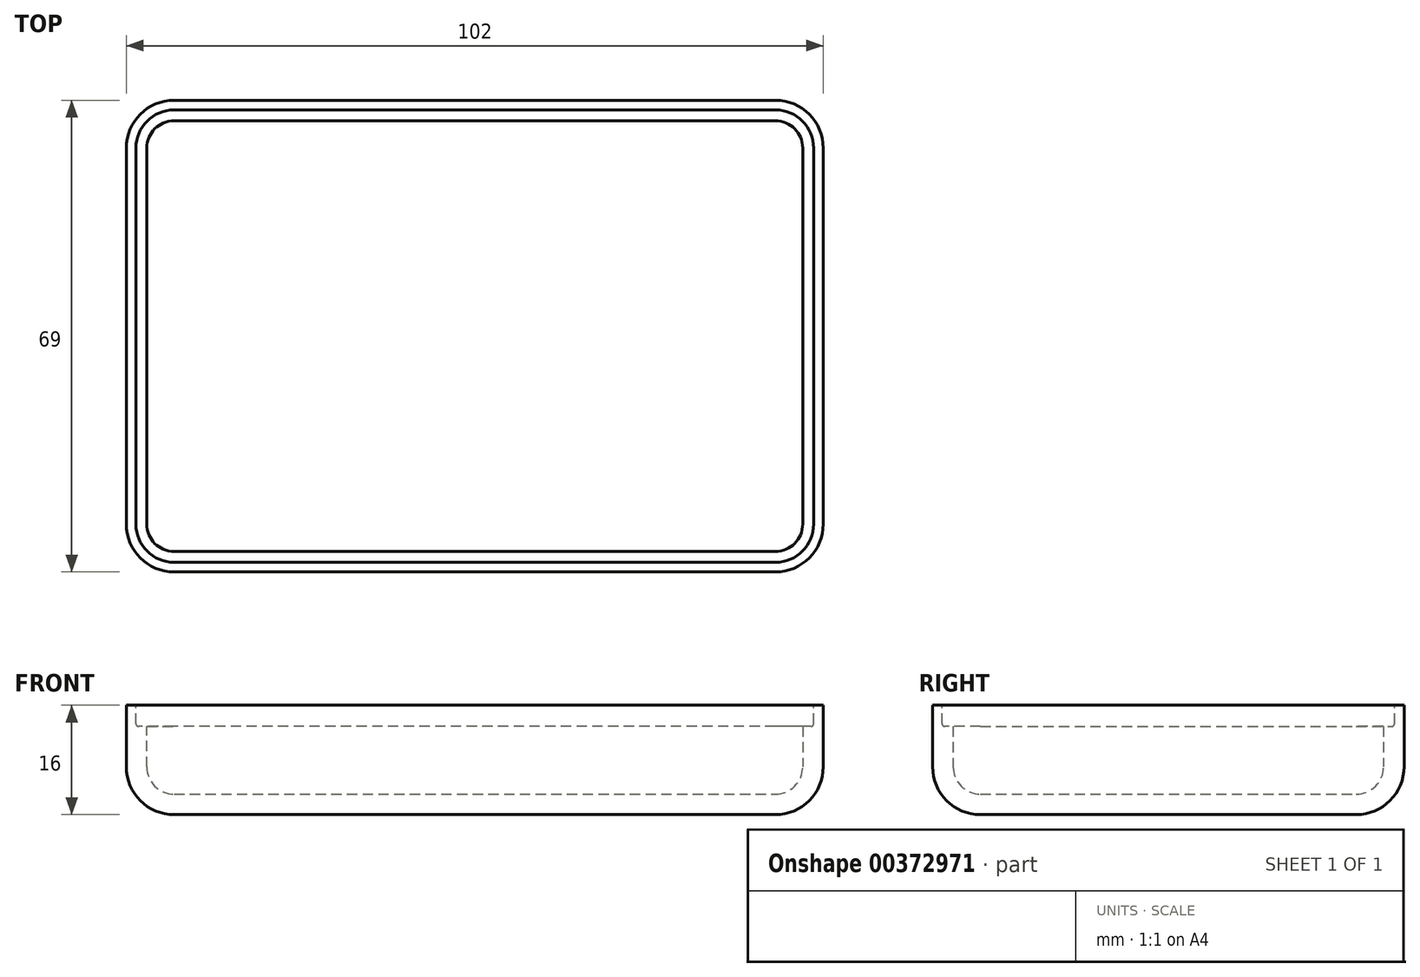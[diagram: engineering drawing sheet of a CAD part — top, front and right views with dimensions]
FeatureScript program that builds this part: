
annotation { "Feature Type Name" : "Feature", "Feature Type Description" : "" }
export const myFeature = defineFeature(function(context is Context, id is Id, definition is map)
    precondition{}
    {
        {
            var Q0;
            Q0=qCreatedBy(makeId("Top.planeOp"),FACE);
            var sketch = newSketch(context, id + "F0", { "sketchPlane" : qUnion([Q0])});
            skLineSegment(sketch, "E0.bottom", {"start": v(44, -34.5) * mm, "end": v(-44, -34.5) * mm});
            skLineSegment(sketch, "E0.top", {"start": v(44, 34.5) * mm, "end": v(-44, 34.5) * mm});
            skLineSegment(sketch, "E0.left", {"start": v(51, -27.5) * mm, "end": v(51, 27.5) * mm});
            skLineSegment(sketch, "E0.right", {"start": v(-51, -27.5) * mm, "end": v(-51, 27.5) * mm});
            skPoint(sketch, "E0.middle", {"position": v(0, 0) * mm});
            skLineSegment(sketch, "E1.bottom", {"start": v(-44, 27.5) * mm, "end": v(44, 27.5) * mm, "construction": true});
            skLineSegment(sketch, "E1.top", {"start": v(-44, -27.5) * mm, "end": v(44, -27.5) * mm, "construction": true});
            skLineSegment(sketch, "E1.left", {"start": v(-44, 27.5) * mm, "end": v(-44, -27.5) * mm, "construction": true});
            skLineSegment(sketch, "E1.right", {"start": v(44, 27.5) * mm, "end": v(44, -27.5) * mm, "construction": true});
            skPoint(sketch, "E2.visualSharp", {"position": v(-51, 34.5) * mm});
            skArc(sketch, "E2.filletArc", {"start": v(-44, 34.5) * mm, "mid": v(-48.95, 32.45) * mm, "end": v(-51, 27.5) * mm});
            skPoint(sketch, "E3.visualSharp", {"position": v(-51, -34.5) * mm});
            skArc(sketch, "E3.filletArc", {"start": v(-51, -27.5) * mm, "mid": v(-48.95, -32.45) * mm, "end": v(-44, -34.5) * mm});
            skPoint(sketch, "E4.visualSharp", {"position": v(51, -34.5) * mm});
            skArc(sketch, "E4.filletArc", {"start": v(44, -34.5) * mm, "mid": v(48.95, -32.45) * mm, "end": v(51, -27.5) * mm});
            skPoint(sketch, "E5.visualSharp", {"position": v(51, 34.5) * mm});
            skArc(sketch, "E5.filletArc", {"start": v(51, 27.5) * mm, "mid": v(48.95, 32.45) * mm, "end": v(44, 34.5) * mm});
            skSolve(sketch);
        }
        {
            var Q0;
            Q0=makeQuery(id+"F0.imprint","IMPRINT",FACE,{"disambiguationData":[TD([[makeQuery(id+"F0.imprint","IMPRINT",EDGE,{"derivedFrom":sQuery(id+"F0.wireOp",EDGE,"E0.bottom")}),-1.0]])]});
            extrude(context, id + "F1", {"entities" : qUnion([Q0]), "depth" : 16 * mm});
        }
        {
            var Q0;
            Q0=makeQuery(id+"F1.opExtrude","CAP_EDGE",EDGE,{"disambiguationData":[OSD([sQuery(id+"F0.wireOp",EDGE,"E0.bottom")])],"isStart":true});
            fillet(context, id + "F2", {"entities" : qUnion([Q0]), "radius" : 7 * mm, "tangentPropagation" : true, "allowEdgeOverflow" : false});
        }
        {
            var Q0;
            Q0=makeQuery(id+"F1.opExtrude","CAP_FACE",FACE,{"disambiguationData":[OSD([sQuery(id+"F0.wireOp",EDGE,"E0.bottom"),sQuery(id+"F0.wireOp",EDGE,"E0.top"),sQuery(id+"F0.wireOp",EDGE,"E0.left"),sQuery(id+"F0.wireOp",EDGE,"E0.right"),sQuery(id+"F0.wireOp",EDGE,"E2.filletArc"),sQuery(id+"F0.wireOp",EDGE,"E3.filletArc"),sQuery(id+"F0.wireOp",EDGE,"E4.filletArc"),sQuery(id+"F0.wireOp",EDGE,"E5.filletArc")])],"isStart":false});
            shell(context, id + "F3", {"entities" : qUnion([Q0]), "thickness" : 3 * mm});
        }
        {
            var Q0;
            Q0=makeQuery(id+"F1.opExtrude","CAP_FACE",FACE,{"disambiguationData":[OSD([sQuery(id+"F0.wireOp",EDGE,"E0.bottom"),sQuery(id+"F0.wireOp",EDGE,"E0.top"),sQuery(id+"F0.wireOp",EDGE,"E0.left"),sQuery(id+"F0.wireOp",EDGE,"E0.right"),sQuery(id+"F0.wireOp",EDGE,"E2.filletArc"),sQuery(id+"F0.wireOp",EDGE,"E3.filletArc"),sQuery(id+"F0.wireOp",EDGE,"E4.filletArc"),sQuery(id+"F0.wireOp",EDGE,"E5.filletArc")])],"isStart":false});
            var sketch = newSketch(context, id + "F4", { "sketchPlane" : qUnion([Q0])});
            skLineSegment(sketch, "E6.0", {"start": v(44, 31.5) * mm, "end": v(-44, 31.5) * mm});
            skArc(sketch, "E7.0", {"start": v(-44, 31.5) * mm, "mid": v(-46.83, 30.33) * mm, "end": v(-48, 27.5) * mm});
            skLineSegment(sketch, "E8.0", {"start": v(-48, -27.5) * mm, "end": v(-48, 27.5) * mm});
            skArc(sketch, "E9.0", {"start": v(-48, -27.5) * mm, "mid": v(-46.83, -30.33) * mm, "end": v(-44, -31.5) * mm});
            skLineSegment(sketch, "E10.0", {"start": v(44, -31.5) * mm, "end": v(-44, -31.5) * mm});
            skArc(sketch, "E11.0", {"start": v(44, -31.5) * mm, "mid": v(46.83, -30.33) * mm, "end": v(48, -27.5) * mm});
            skLineSegment(sketch, "E12.0", {"start": v(48, -27.5) * mm, "end": v(48, 27.5) * mm});
            skArc(sketch, "E13.0", {"start": v(48, 27.5) * mm, "mid": v(46.83, 30.33) * mm, "end": v(44, 31.5) * mm});
            skArc(sketch, "E14.0", {"start": v(49.6, 27.5) * mm, "mid": v(47.96, 31.46) * mm, "end": v(44, 33.1) * mm});
            skLineSegment(sketch, "E14.1", {"start": v(49.6, -27.5) * mm, "end": v(49.6, 27.5) * mm});
            skLineSegment(sketch, "E14.2", {"start": v(44, 33.1) * mm, "end": v(-44, 33.1) * mm});
            skArc(sketch, "E14.3", {"start": v(44, -33.1) * mm, "mid": v(47.96, -31.46) * mm, "end": v(49.6, -27.5) * mm});
            skArc(sketch, "E14.4", {"start": v(-44, 33.1) * mm, "mid": v(-47.96, 31.46) * mm, "end": v(-49.6, 27.5) * mm});
            skLineSegment(sketch, "E14.5", {"start": v(-49.6, -27.5) * mm, "end": v(-49.6, 27.5) * mm});
            skArc(sketch, "E14.6", {"start": v(-49.6, -27.5) * mm, "mid": v(-47.96, -31.46) * mm, "end": v(-44, -33.1) * mm});
            skLineSegment(sketch, "E14.7", {"start": v(44, -33.1) * mm, "end": v(-44, -33.1) * mm});
            skSolve(sketch);
        }
        {
            var Q0;
            Q0 = qSketchRegion(id + "F4", true);
            extrude(context, id + "F5", {"entities" : qUnion([Q0]), "operationType" : NewBodyOperationType.REMOVE, "oppositeDirection" : true, "depth" : 3.1 * mm});
        }
        {
            var Q0;
            Q0=makeQuery(id+"F5.boolean.opBoolean","COPY",EDGE,{"derivedFrom":makeQuery(id+"F5.opExtrude","CAP_EDGE",EDGE,{"disambiguationData":[OSD([sQuery(id+"F4.wireOp",EDGE,"E14.2")])],"isStart":false})});
            var Q1;
            Q1=makeQuery(id+"F5.boolean.opBoolean","COPY",EDGE,{"derivedFrom":makeQuery(id+"F5.opExtrude","CAP_EDGE",EDGE,{"disambiguationData":[OSD([sQuery(id+"F4.wireOp",EDGE,"E14.7")])],"isStart":true})});
            fillet(context, id + "F6", {"entities" : qUnion([Q0, Q1]), "radius" : 0.4 * mm, "tangentPropagation" : true, "allowEdgeOverflow" : false});
        }
    });
